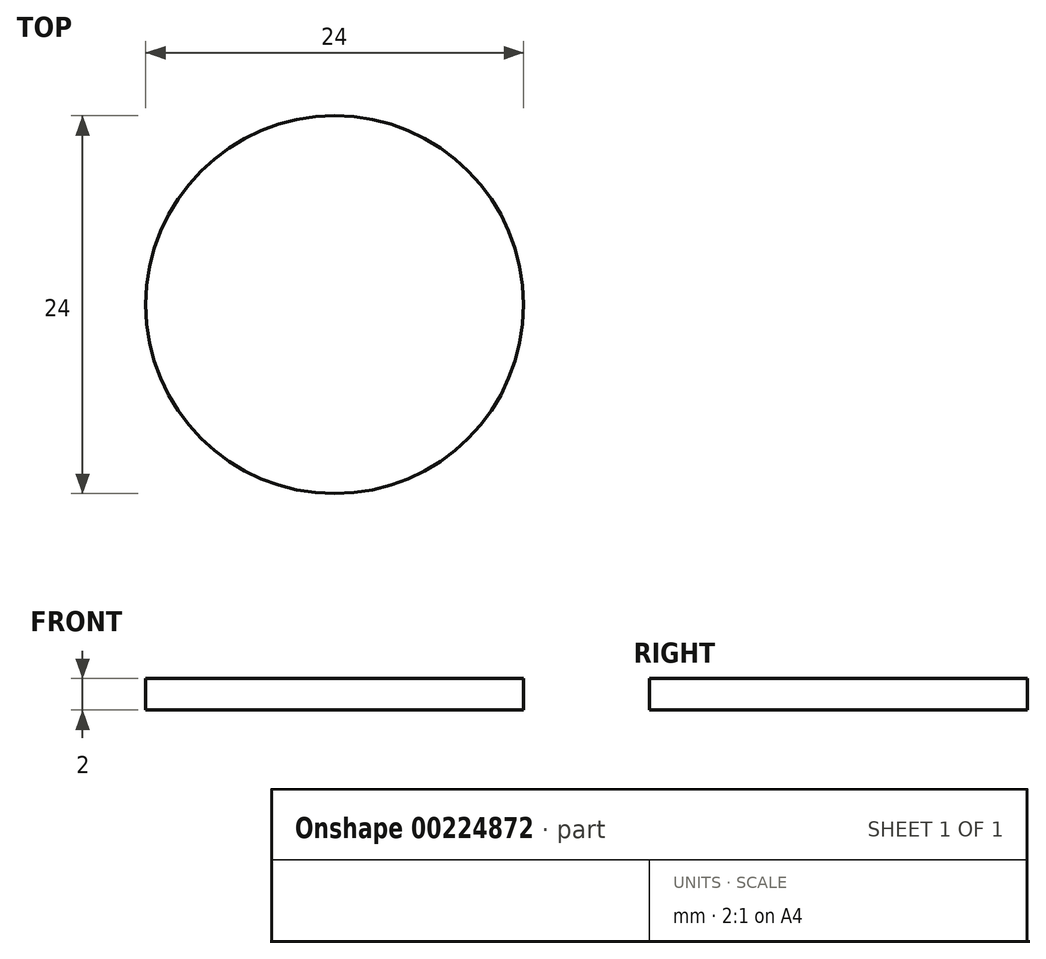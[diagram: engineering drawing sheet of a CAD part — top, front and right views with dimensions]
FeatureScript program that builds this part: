
annotation { "Feature Type Name" : "Feature", "Feature Type Description" : "" }
export const myFeature = defineFeature(function(context is Context, id is Id, definition is map)
    precondition{}
    {
        {
            var Q0;
            Q0=qCreatedBy(makeId("Right.planeOp"),FACE);
            var sketch = newSketch(context, id + "F0", { "sketchPlane" : qUnion([Q0])});
            skLineSegment(sketch, "E0", {"start": v(-10, 6.34) * mm, "end": v(-12, 6.34) * mm});
            skLineSegment(sketch, "E1", {"start": v(-12, 6.34) * mm, "end": v(-12, 8.34) * mm});
            skLineSegment(sketch, "E2", {"start": v(-12, 8.34) * mm, "end": v(0, 8.34) * mm});
            skLineSegment(sketch, "E3", {"start": v(0, 6.34) * mm, "end": v(0, 8.34) * mm});
            skLineSegment(sketch, "E4", {"start": v(-10, 6.34) * mm, "end": v(0, 6.34) * mm});
            skPoint(sketch, "E5.orphan", {"position": v(0, -5.66) * mm});
            skSolve(sketch);
        }
        {
            var Q0;
            Q0=makeQuery(id+"F0.imprint","IMPRINT",FACE,{"disambiguationData":[TD([[makeQuery(id+"F0.imprint","IMPRINT",EDGE,{"derivedFrom":sQuery(id+"F0.wireOp",EDGE,"E0")}),-1.0]])]});
            var Q1;
            Q1=sQuery(id+"F0.wireOp",EDGE,"E3");
            revolve(context, id + "F1", {"entities" : qUnion([Q0]), "axis" : qUnion([Q1]), "revolveType" : RevolveType.FULL});
        }
    });
